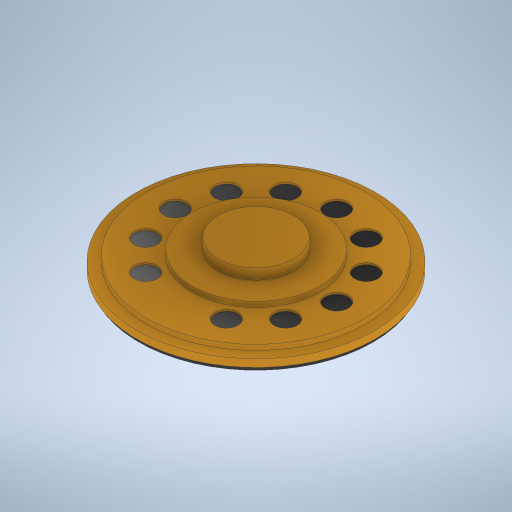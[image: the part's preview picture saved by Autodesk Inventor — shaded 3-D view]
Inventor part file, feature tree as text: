
AUTODESK INVENTOR PART (.ipt)
format: ipt  version: 2023 (Build 270158000, 158)  size: 384,512 bytes
history: native  units: mm
features: sketch x6, extrude x4, other x1, revolve x1, pattern_circular x1
ambient origin geometry x8: Origin, YZ Plane, XZ Plane, XY Plane, X Axis, Y Axis, Z Axis, Center Point
bodies: Body1 (feature_tree)
feature tree (13):
  other  "솔리드1"
  revolve  "회전1"
  extrude  "돌출1"  Depth=28.5mm
  extrude  "돌출2"  Depth=2.8mm
  sketch  "스케치4"
  extrude  "돌출3"  Depth=26.075mm
  pattern_circular  "원형 패턴1"  [2 undecoded]
  extrude  "돌출4"  Depth=1.8mm
  sketch  "스케치1"
  sketch  "스케치2"
  sketch  "스케치3"
  sketch  "스케치5"
  sketch  "스케치6"
note: 2 required parameter values undecoded (feature->parameter linkage not recoverable at this tier; creation-order binding heuristic only, values carry confidence <= 0.55)
